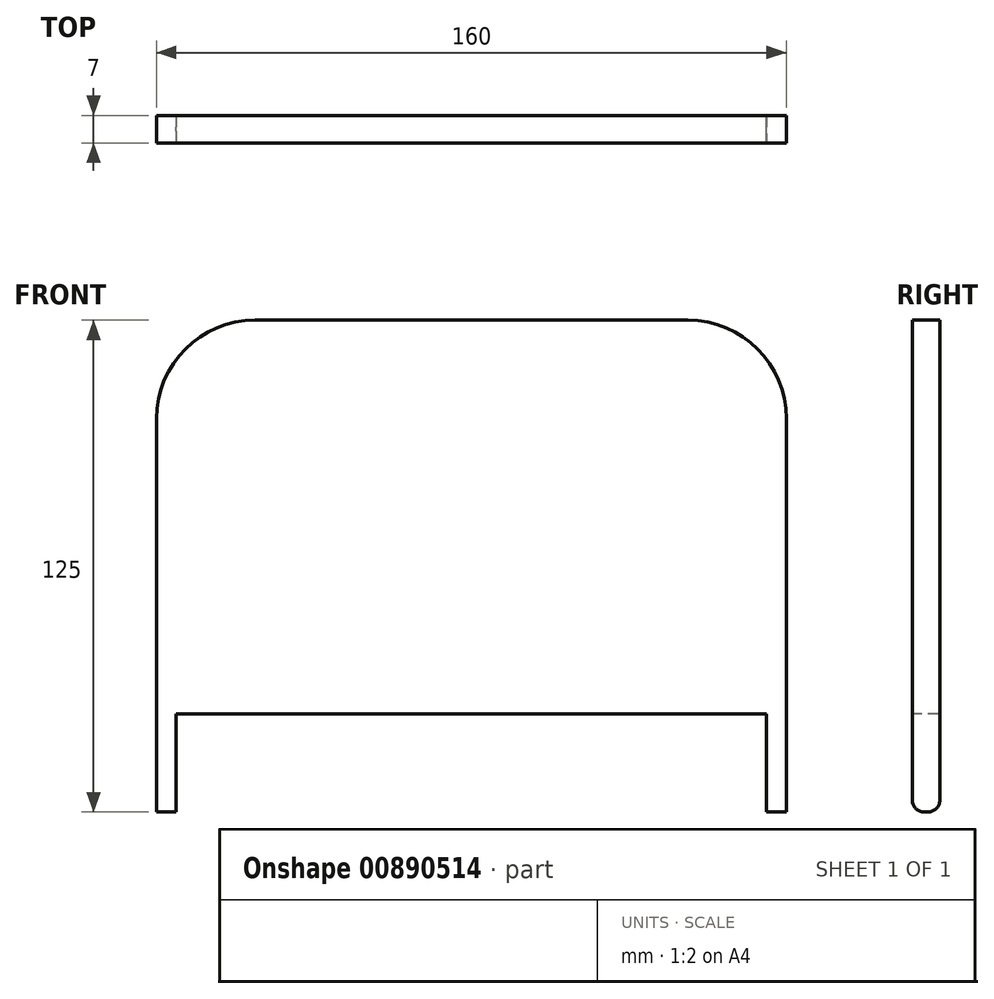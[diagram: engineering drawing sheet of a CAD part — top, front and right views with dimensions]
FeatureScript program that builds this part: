
annotation { "Feature Type Name" : "Feature", "Feature Type Description" : "" }
export const myFeature = defineFeature(function(context is Context, id is Id, definition is map)
    precondition{}
    {
        {
            var Q0;
            Q0=qCreatedBy(makeId("Right.planeOp"),FACE);
            var sketch = newSketch(context, id + "F0", { "sketchPlane" : qUnion([Q0])});
            skLineSegment(sketch, "E0.bottom", {"start": v(3.5, 50) * mm, "end": v(-3.5, 50) * mm});
            skLineSegment(sketch, "E0.top", {"start": v(3.5, -50) * mm, "end": v(-3.5, -50) * mm});
            skLineSegment(sketch, "E0.left", {"start": v(3.5, 50) * mm, "end": v(3.5, -50) * mm});
            skLineSegment(sketch, "E0.right", {"start": v(-3.5, 50) * mm, "end": v(-3.5, -50) * mm});
            skPoint(sketch, "E0.middle", {"position": v(0, 0) * mm});
            skSolve(sketch);
        }
        {
            var Q0;
            Q0=makeQuery(id+"F0.imprint","IMPRINT",FACE,{"disambiguationData":[TD([[makeQuery(id+"F0.imprint","IMPRINT",EDGE,{"derivedFrom":sQuery(id+"F0.wireOp",EDGE,"E0.bottom")}),1.0]])]});
            extrude(context, id + "F1", {"entities" : qUnion([Q0]), "depth" : 75 * mm, "offsetDistance" : 25 * mm, "hasSecondDirection" : true, "secondDirectionOppositeDirection" : true, "secondDirectionDepth" : 75 * mm});
        }
        {
            var Q0;
            Q0=makeQuery(id+"F1.opExtrude","CAP_FACE",FACE,{"disambiguationData":[OSD([sQuery(id+"F0.wireOp",EDGE,"E0.bottom"),sQuery(id+"F0.wireOp",EDGE,"E0.top"),sQuery(id+"F0.wireOp",EDGE,"E0.left"),sQuery(id+"F0.wireOp",EDGE,"E0.right")])],"isStart":false});
            var sketch = newSketch(context, id + "F2", { "sketchPlane" : qUnion([Q0])});
            skLineSegment(sketch, "E1", {"start": v(-3.5, 50) * mm, "end": v(-3.5, -75) * mm});
            skLineSegment(sketch, "E2", {"start": v(-3.5, -75) * mm, "end": v(3.5, -75) * mm});
            skLineSegment(sketch, "E3", {"start": v(3.5, -75) * mm, "end": v(3.5, 50) * mm});
            skLineSegment(sketch, "E4", {"start": v(3.5, 50) * mm, "end": v(-3.5, 50) * mm});
            skSolve(sketch);
        }
        {
            var Q0;
            Q0=qSketchRegion(id+"F2",true);
            extrude(context, id + "F3", {"entities" : qUnion([Q0]), "operationType" : NewBodyOperationType.ADD, "depth" : 5 * mm, "offsetDistance" : 25 * mm});
        }
        {
            var Q0;
            Q0=makeQuery(id+"F1.opExtrude","SWEPT_BODY",BODY,{"disambiguationData":[OSD([sQuery(id+"F0.wireOp",EDGE,"E0.bottom"),sQuery(id+"F0.wireOp",EDGE,"E0.top"),sQuery(id+"F0.wireOp",EDGE,"E0.left"),sQuery(id+"F0.wireOp",EDGE,"E0.right")])]});
            var Q1;
            Q1=qCreatedBy(makeId("Right.planeOp"),FACE);
            mirror(context, id + "F4", {"operationType" : NewBodyOperationType.ADD, "entities" : qUnion([Q0]), "mirrorPlane" : qUnion([Q1])});
        }
        {
            var Q0;
            Q0=makeQuery(id+"F4.opPattern","COPY",EDGE,{"derivedFrom":makeQuery(id+"F3.opExtrude","CAP_EDGE",EDGE,{"disambiguationData":[OSD([sQuery(id+"F2.wireOp",EDGE,"E4")])],"isStart":false}),"instanceName":"1"});
            var Q1;
            Q1=makeQuery(id+"F3.opExtrude","CAP_EDGE",EDGE,{"disambiguationData":[OSD([sQuery(id+"F2.wireOp",EDGE,"E4")])],"isStart":false});
            fillet(context, id + "F5", {"entities" : qUnion([Q0, Q1]), "radius" : 25 * mm, "tangentPropagation" : true, "allowEdgeOverflow" : false});
        }
        {
            var Q0;
            Q0=makeQuery(id+"F4.opPattern","COPY",EDGE,{"derivedFrom":makeQuery(id+"F3.opExtrude","SWEPT_EDGE",EDGE,{"disambiguationData":[OSD([sQuery(id+"F2.wireOp",EDGE,"E1"),sQuery(id+"F2.wireOp",EDGE,"E2")])]}),"instanceName":"1"});
            var Q1;
            Q1=makeQuery(id+"F3.opExtrude","SWEPT_EDGE",EDGE,{"disambiguationData":[OSD([sQuery(id+"F2.wireOp",EDGE,"E1"),sQuery(id+"F2.wireOp",EDGE,"E2")])]});
            var Q2;
            Q2=makeQuery(id+"F4.opPattern","COPY",EDGE,{"derivedFrom":makeQuery(id+"F3.opExtrude","SWEPT_EDGE",EDGE,{"disambiguationData":[OSD([sQuery(id+"F2.wireOp",EDGE,"E2"),sQuery(id+"F2.wireOp",EDGE,"E3")])]}),"instanceName":"1"});
            var Q3;
            Q3=makeQuery(id+"F3.opExtrude","SWEPT_EDGE",EDGE,{"disambiguationData":[OSD([sQuery(id+"F2.wireOp",EDGE,"E2"),sQuery(id+"F2.wireOp",EDGE,"E3")])]});
            fillet(context, id + "F6", {"entities" : qUnion([Q0, Q1, Q2, Q3]), "radius" : 3 * mm, "tangentPropagation" : true, "allowEdgeOverflow" : false});
        }
    });
